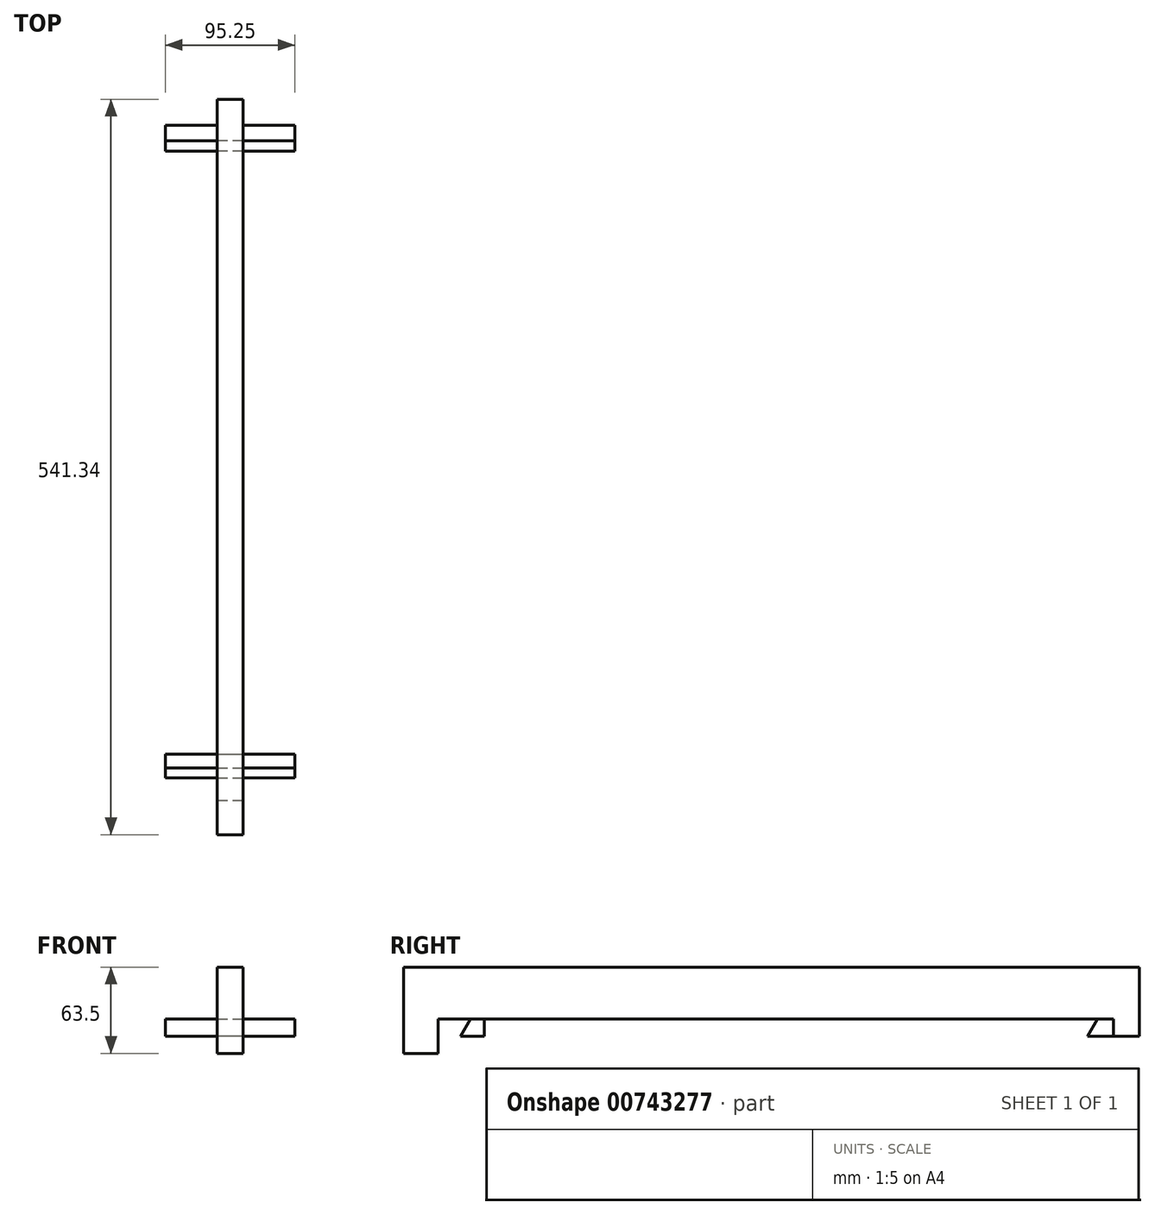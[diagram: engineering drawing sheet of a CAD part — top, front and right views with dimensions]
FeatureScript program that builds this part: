
annotation { "Feature Type Name" : "Feature", "Feature Type Description" : "" }
export const myFeature = defineFeature(function(context is Context, id is Id, definition is map)
    precondition{}
    {
        {
            var Q0;
            Q0=qCreatedBy(makeId("Right.planeOp"),FACE);
            var sketch = newSketch(context, id + "F0", { "sketchPlane" : qUnion([Q0])});
            skLineSegment(sketch, "E0", {"start": v(0, 0) * mm, "end": v(0, 50.8) * mm});
            skLineSegment(sketch, "E1", {"start": v(0, 50.8) * mm, "end": v(-477.84, 50.8) * mm});
            skLineSegment(sketch, "E2", {"start": v(-477.84, 50.8) * mm, "end": v(-477.84, 12.7) * mm});
            skLineSegment(sketch, "E3", {"start": v(0, 0) * mm, "end": v(-19.05, 0) * mm});
            skLineSegment(sketch, "E4", {"start": v(-19.05, 0) * mm, "end": v(-11.72, 12.7) * mm});
            skLineSegment(sketch, "E5", {"start": v(-11.72, 12.7) * mm, "end": v(-477.84, 12.7) * mm});
            skSolve(sketch);
        }
        {
            var Q0;
            Q0=makeQuery(id+"F0.imprint","IMPRINT",FACE,{"disambiguationData":[TD([[makeQuery(id+"F0.imprint","IMPRINT",EDGE,{"derivedFrom":sQuery(id+"F0.wireOp",EDGE,"E0")}),1.0]])]});
            extrude(context, id + "F1", {"entities" : qUnion([Q0]), "depth" : 19.05 * mm, "offsetDistance" : 25.4 * mm});
        }
        {
            var Q0;
            Q0=makeQuery(id+"F1.opExtrude","CAP_FACE",FACE,{"disambiguationData":[OSD([sQuery(id+"F0.wireOp",EDGE,"E0"),sQuery(id+"F0.wireOp",EDGE,"E1"),sQuery(id+"F0.wireOp",EDGE,"E2"),sQuery(id+"F0.wireOp",EDGE,"E3"),sQuery(id+"F0.wireOp",EDGE,"E4"),sQuery(id+"F0.wireOp",EDGE,"E5")])],"isStart":false});
            var sketch = newSketch(context, id + "F2", { "sketchPlane" : qUnion([Q0])});
            skLineSegment(sketch, "E6", {"start": v(-11.72, 12.7) * mm, "end": v(-19.05, 0) * mm});
            skLineSegment(sketch, "E7", {"start": v(-19.05, 0) * mm, "end": v(0, 0) * mm});
            skLineSegment(sketch, "E8", {"start": v(0, 0) * mm, "end": v(0, 12.7) * mm});
            skLineSegment(sketch, "E9", {"start": v(0, 12.7) * mm, "end": v(-11.72, 12.7) * mm});
            skSolve(sketch);
        }
        {
            var Q0;
            Q0=makeQuery(id+"F2.imprint","IMPRINT",FACE,{"disambiguationData":[TD([[makeQuery(id+"F2.imprint","IMPRINT",EDGE,{"derivedFrom":sQuery(id+"F2.wireOp",EDGE,"E6")}),-1.0]])]});
            var Q1;
            {var subQ0=sQuery(id+"F2.wireOp",EDGE,"E6");Q1=makeQuery(id+"F2.imprint","IMPRINT",FACE,{"disambiguationData":[TD([[makeQuery(id+"F2.imprint","IMPRINT",EDGE,{"derivedFrom":subQ0}),1.0]])]});}
            var Q2;
            {var subQ0=sQuery(id+"F2.wireOp",EDGE,"E8");Q2=makeQuery(id+"F2.imprint","IMPRINT",FACE,{"disambiguationData":[TD([[makeQuery(id+"F2.imprint","IMPRINT",EDGE,{"derivedFrom":subQ0}),1.0]])]});}
            extrude(context, id + "F3", {"entities" : qUnion([Q0, Q1, Q2]), "operationType" : NewBodyOperationType.ADD, "depth" : 38.1 * mm, "offsetDistance" : 25.4 * mm});
        }
        {
            var Q0;
            Q0=makeQuery(id+"F1.opExtrude","CAP_FACE",FACE,{"disambiguationData":[OSD([sQuery(id+"F0.wireOp",EDGE,"E0"),sQuery(id+"F0.wireOp",EDGE,"E1"),sQuery(id+"F0.wireOp",EDGE,"E2"),sQuery(id+"F0.wireOp",EDGE,"E3"),sQuery(id+"F0.wireOp",EDGE,"E4"),sQuery(id+"F0.wireOp",EDGE,"E5")])],"isStart":true});
            var sketch = newSketch(context, id + "F4", { "sketchPlane" : qUnion([Q0])});
            skLineSegment(sketch, "E10", {"start": v(11.72, 12.7) * mm, "end": v(19.05, 0) * mm});
            skLineSegment(sketch, "E11", {"start": v(19.05, 0) * mm, "end": v(0, 0) * mm});
            skLineSegment(sketch, "E12", {"start": v(0, 0) * mm, "end": v(0, 12.7) * mm});
            skLineSegment(sketch, "E13", {"start": v(0, 12.7) * mm, "end": v(11.72, 12.7) * mm});
            skSolve(sketch);
        }
        {
            var Q0;
            Q0=makeQuery(id+"F4.imprint","IMPRINT",FACE,{"disambiguationData":[TD([[makeQuery(id+"F4.imprint","IMPRINT",EDGE,{"derivedFrom":sQuery(id+"F4.wireOp",EDGE,"E10")}),1.0]])]});
            var Q1;
            Q1=makeQuery(id+"F3.opExtrude","CAP_FACE",FACE,{"disambiguationData":[OSD([sQuery(id+"F2.wireOp",EDGE,"E6"),sQuery(id+"F2.wireOp",EDGE,"E7"),sQuery(id+"F2.wireOp",EDGE,"E8"),sQuery(id+"F2.wireOp",EDGE,"E9")])],"isStart":true});
            extrude(context, id + "F5", {"entities" : qUnion([Q0, Q1]), "operationType" : NewBodyOperationType.ADD, "depth" : 38.1 * mm, "offsetDistance" : 25.4 * mm});
        }
        {
            var Q0;
            Q0=makeQuery(id+"F5.boolean.opBoolean","MERGE",FACE,{"derivedFrom":[makeQuery(id+"F3.boolean.opBoolean","MERGE",FACE,{"derivedFrom":[makeQuery(id+"F1.opExtrude","SWEPT_FACE",FACE,{"disambiguationData":[OSD([sQuery(id+"F0.wireOp",EDGE,"E0")])]}),makeQuery(id+"F3.opExtrude","SWEPT_FACE",FACE,{"disambiguationData":[OSD([sQuery(id+"F2.wireOp",EDGE,"E8")])]})]}),makeQuery(id+"F5.opExtrude","SWEPT_FACE",FACE,{"disambiguationData":[OSD([sQuery(id+"F4.wireOp",EDGE,"E12")])]})]});
            var sketch = newSketch(context, id + "F6", { "sketchPlane" : qUnion([Q0])});
            skLineSegment(sketch, "E14.bottom", {"start": v(-19.05, 50.8) * mm, "end": v(0, 50.8) * mm});
            skLineSegment(sketch, "E14.top", {"start": v(-19.05, 0) * mm, "end": v(0, 0) * mm});
            skLineSegment(sketch, "E14.left", {"start": v(-19.05, 50.8) * mm, "end": v(-19.05, 0) * mm});
            skLineSegment(sketch, "E14.right", {"start": v(0, 50.8) * mm, "end": v(0, 0) * mm});
            skSolve(sketch);
        }
        {
            var Q0;
            {var subQ7=sQuery(id+"F6.wireOp",EDGE,"E14.bottom");Q0=makeQuery(id+"F6.imprint","IMPRINT",FACE,{"disambiguationData":[TD([[makeQuery(id+"F6.imprint","IMPRINT",EDGE,{"derivedFrom":subQ7}),-1.0]])]});}
            extrude(context, id + "F7", {"entities" : qUnion([Q0]), "operationType" : NewBodyOperationType.ADD, "depth" : 19.05 * mm, "offsetDistance" : 25.4 * mm});
        }
        {
            var Q0;
            Q0=makeQuery(id+"F7.boolean.opBoolean","MERGE",FACE,{"derivedFrom":[makeQuery(id+"F1.opExtrude","CAP_FACE",FACE,{"disambiguationData":[OSD([sQuery(id+"F0.wireOp",EDGE,"E0"),sQuery(id+"F0.wireOp",EDGE,"E1"),sQuery(id+"F0.wireOp",EDGE,"E2"),sQuery(id+"F0.wireOp",EDGE,"E3"),sQuery(id+"F0.wireOp",EDGE,"E4"),sQuery(id+"F0.wireOp",EDGE,"E5")])],"isStart":false}),makeQuery(id+"F7.opExtrude","SWEPT_FACE",FACE,{"disambiguationData":[OSD([sQuery(id+"F6.wireOp",EDGE,"E14.left")])]})]});
            var sketch = newSketch(context, id + "F8", { "sketchPlane" : qUnion([Q0])});
            skLineSegment(sketch, "E15", {"start": v(-473.08, 12.7) * mm, "end": v(-480.4, 0) * mm});
            skLineSegment(sketch, "E16", {"start": v(-480.4, 0) * mm, "end": v(-462.94, 0) * mm});
            skLineSegment(sketch, "E17", {"start": v(-462.94, 0) * mm, "end": v(-462.94, 12.7) * mm});
            skLineSegment(sketch, "E18", {"start": v(-462.94, 12.7) * mm, "end": v(-473.08, 12.7) * mm});
            skSolve(sketch);
        }
        {
            var Q0;
            Q0=makeQuery(id+"F8.imprint","IMPRINT",FACE,{"disambiguationData":[TD([[makeQuery(id+"F8.imprint","IMPRINT",EDGE,{"derivedFrom":sQuery(id+"F8.wireOp",EDGE,"E15")}),1.0]])]});
            extrude(context, id + "F9", {"entities" : qUnion([Q0]), "operationType" : NewBodyOperationType.ADD, "oppositeDirection" : true, "depth" : 57.15 * mm, "offsetDistance" : 25.4 * mm});
        }
        {
            var Q0;
            Q0 = qSketchRegion(id + "F8", true);
            extrude(context, id + "F10", {"entities" : qUnion([Q0]), "operationType" : NewBodyOperationType.ADD, "depth" : 38.1 * mm, "offsetDistance" : 25.4 * mm});
        }
        {
            var Q0;
            Q0=makeQuery(id+"F1.opExtrude","SWEPT_FACE",FACE,{"disambiguationData":[OSD([sQuery(id+"F0.wireOp",EDGE,"E2")])]});
            var sketch = newSketch(context, id + "F11", { "sketchPlane" : qUnion([Q0])});
            skLineSegment(sketch, "E19.bottom", {"start": v(0, 50.8) * mm, "end": v(19.05, 50.8) * mm});
            skLineSegment(sketch, "E19.top", {"start": v(0, 12.7) * mm, "end": v(19.05, 12.7) * mm});
            skLineSegment(sketch, "E19.left", {"start": v(0, 50.8) * mm, "end": v(0, 12.7) * mm});
            skLineSegment(sketch, "E19.right", {"start": v(19.05, 50.8) * mm, "end": v(19.05, 12.7) * mm});
            skSolve(sketch);
        }
        {
            var Q0;
            Q0 = qSketchRegion(id + "F11", true);
            extrude(context, id + "F12", {"entities" : qUnion([Q0]), "operationType" : NewBodyOperationType.ADD, "depth" : 25.4 * mm, "offsetDistance" : 25.4 * mm});
        }
        {
            var Q0;
            Q0=makeQuery(id+"F12.opExtrude","SWEPT_FACE",FACE,{"disambiguationData":[OSD([sQuery(id+"F11.wireOp",EDGE,"E19.top")])]});
            var sketch = newSketch(context, id + "F13", { "sketchPlane" : qUnion([Q0])});
            skLineSegment(sketch, "E20.bottom", {"start": v(0, 496.89) * mm, "end": v(19.05, 496.89) * mm});
            skLineSegment(sketch, "E20.top", {"start": v(0, 522.29) * mm, "end": v(19.05, 522.29) * mm});
            skLineSegment(sketch, "E20.left", {"start": v(0, 496.89) * mm, "end": v(0, 522.29) * mm});
            skLineSegment(sketch, "E20.right", {"start": v(19.05, 496.89) * mm, "end": v(19.05, 522.29) * mm});
            skSolve(sketch);
        }
        {
            var Q0;
            {var subQ0=sQuery(id+"F13.wireOp",EDGE,"E20.top");Q0=makeQuery(id+"F13.imprint","IMPRINT",FACE,{"disambiguationData":[TD([[makeQuery(id+"F13.imprint","IMPRINT",EDGE,{"derivedFrom":subQ0}),-1.0]])]});}
            var Q1;
            {var subQ0=sQuery(id+"F13.wireOp",EDGE,"E20.bottom");Q1=makeQuery(id+"F13.imprint","IMPRINT",FACE,{"disambiguationData":[TD([[makeQuery(id+"F13.imprint","IMPRINT",EDGE,{"derivedFrom":subQ0}),1.0]])]});}
            extrude(context, id + "F14", {"entities" : qUnion([Q0, Q1]), "operationType" : NewBodyOperationType.ADD, "depth" : 25.4 * mm, "offsetDistance" : 25.4 * mm});
        }
        {
            var Q0;
            Q0=makeQuery(id+"F14.opExtrude","CAP_FACE",FACE,{"disambiguationData":[OSD([sQuery(id+"F13.wireOp",EDGE,"E20.bottom"),sQuery(id+"F13.wireOp",EDGE,"E20.top"),sQuery(id+"F13.wireOp",EDGE,"E20.left"),sQuery(id+"F13.wireOp",EDGE,"E20.right")])],"isStart":true});
            var Q1;
            Q1=makeQuery(id+"F12.boolean.opBoolean","MERGE",FACE,{"derivedFrom":[makeQuery(id+"F7.boolean.opBoolean","MERGE",FACE,{"derivedFrom":[makeQuery(id+"F1.opExtrude","SWEPT_FACE",FACE,{"disambiguationData":[OSD([sQuery(id+"F0.wireOp",EDGE,"E1")])]}),makeQuery(id+"F7.opExtrude","SWEPT_FACE",FACE,{"disambiguationData":[OSD([sQuery(id+"F6.wireOp",EDGE,"E14.bottom")])]})]}),makeQuery(id+"F12.opExtrude","SWEPT_FACE",FACE,{"disambiguationData":[OSD([sQuery(id+"F11.wireOp",EDGE,"E19.bottom")])]})]});
            extrude(context, id + "F15", {"entities" : qUnion([Q0]), "operationType" : NewBodyOperationType.ADD, "endBound" : BoundingType.UP_TO_SURFACE, "depth" : 25.4 * mm, "endBoundEntityFace" : qUnion([Q1]), "offsetDistance" : 25.4 * mm});
        }
    });
